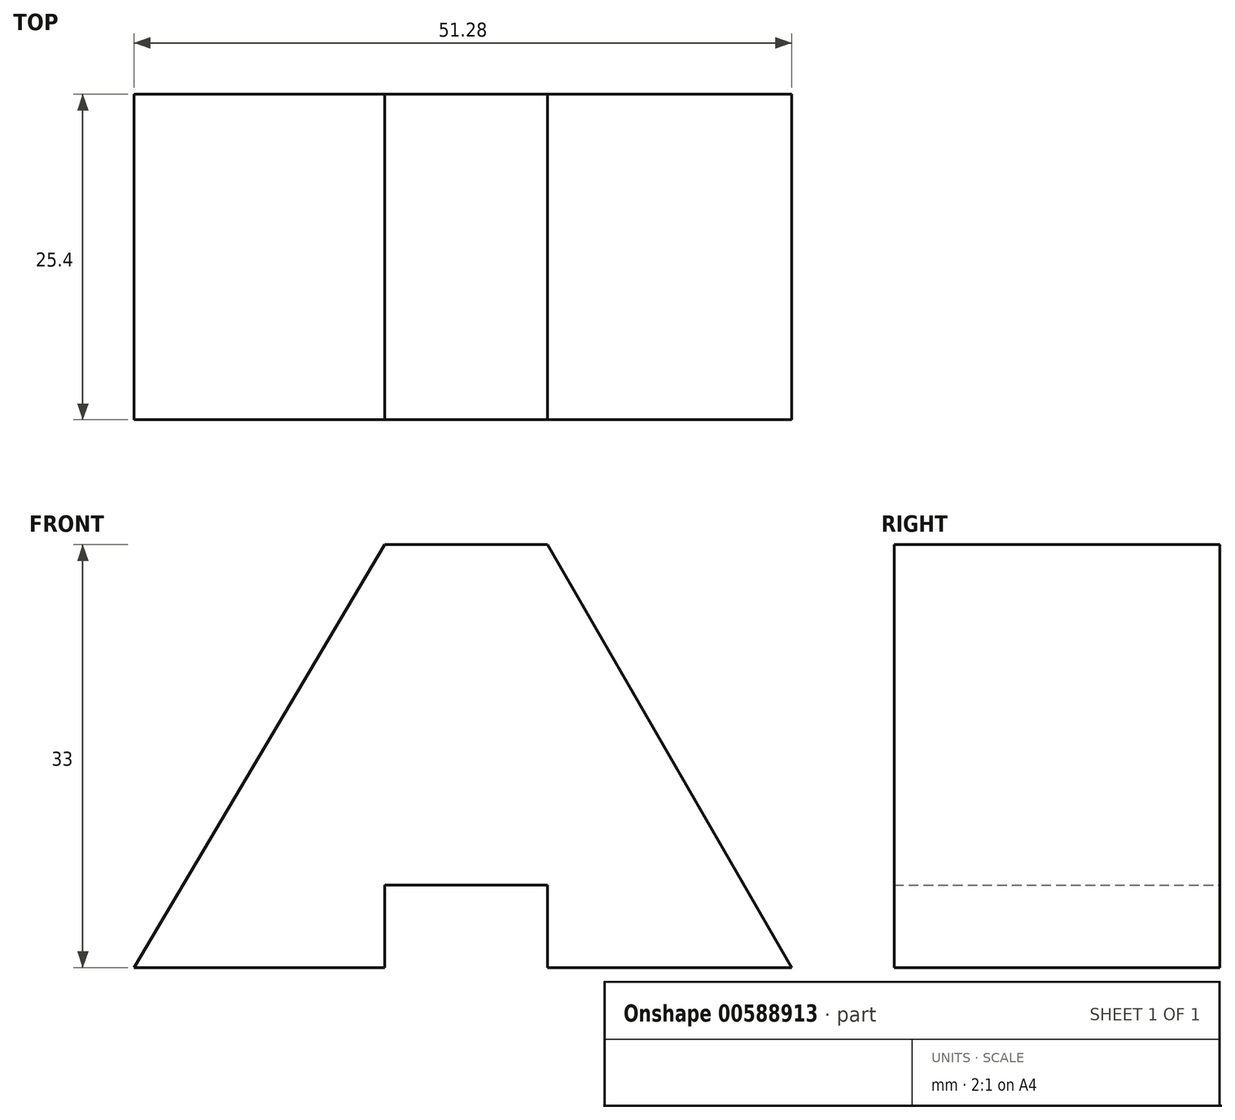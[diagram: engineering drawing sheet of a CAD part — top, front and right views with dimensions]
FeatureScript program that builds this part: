
annotation { "Feature Type Name" : "Feature", "Feature Type Description" : "" }
export const myFeature = defineFeature(function(context is Context, id is Id, definition is map)
    precondition{}
    {
        {
            var Q0;
            Q0=qCreatedBy(makeId("Front.planeOp"),FACE);
            var sketch = newSketch(context, id + "F0", { "sketchPlane" : qUnion([Q0])});
            skLineSegment(sketch, "E0", {"start": v(-64.38, 0) * mm, "end": v(-44.85, 33) * mm});
            skLineSegment(sketch, "E1", {"start": v(-44.85, 33) * mm, "end": v(-32.15, 33) * mm});
            skLineSegment(sketch, "E2", {"start": v(-32.15, 33) * mm, "end": v(-13.1, 0) * mm});
            skLineSegment(sketch, "E3", {"start": v(-64.38, 0) * mm, "end": v(-44.85, 0) * mm});
            skLineSegment(sketch, "E4", {"start": v(-44.85, 0) * mm, "end": v(-44.85, 6.44) * mm});
            skLineSegment(sketch, "E5", {"start": v(-44.85, 6.44) * mm, "end": v(-32.15, 6.44) * mm});
            skLineSegment(sketch, "E6", {"start": v(-32.15, 6.44) * mm, "end": v(-32.15, 0) * mm});
            skLineSegment(sketch, "E7", {"start": v(-32.15, 0) * mm, "end": v(-13.1, 0) * mm});
            skSolve(sketch);
        }
        {
            var Q0;
            Q0=makeQuery(id+"F0.imprint","IMPRINT",FACE,{"disambiguationData":[TD([[makeQuery(id+"F0.imprint","IMPRINT",EDGE,{"derivedFrom":sQuery(id+"F0.wireOp",EDGE,"E0")}),-1.0]])]});
            extrude(context, id + "F1", {"entities" : qUnion([Q0]), "depth" : 25.4 * mm, "offsetDistance" : 25.4 * mm});
        }
    });
